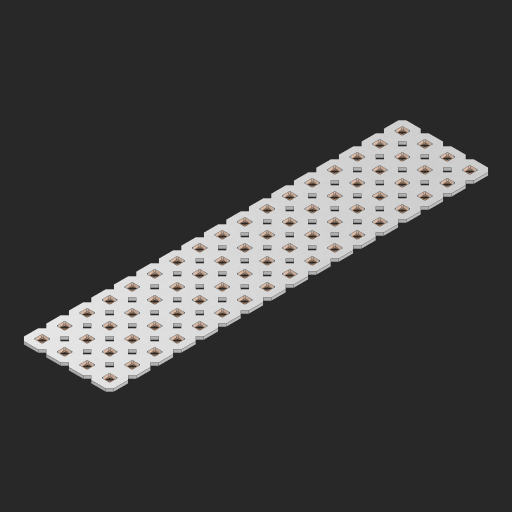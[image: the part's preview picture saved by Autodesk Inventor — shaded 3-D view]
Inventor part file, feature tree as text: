
AUTODESK INVENTOR PART (.ipt)
format: ipt  version: 2023 (Build 270158000, 158)  size: 1,068,544 bytes
history: native  units: in
note: dims shown in document units (in); Inventor stores cm internally (conversion verified against a paired STEP export)
features: other x69, extrude x67, sketch x2, pattern_linear x1
ambient origin geometry x8: Origin, YZ Plane, XZ Plane, XY Plane, X Axis, Y Axis, Z Axis, Center Point
bodies: Solid1 (feature_tree), Body (feature_tree)
feature tree (139):
  pattern_linear  "Rectangular Pattern1"  Spacing1=0.09in  [1 undecoded]
  sketch  "Sketch1"  dims[d1=0.5in]
  sketch  "Sketch2"  dims[d2=0.182in d3=0.09in d4=0.09in d5=0.09in d6=0.09in d7=0.09in d8=0.09in d9=0.09in d10=0.09in d11=0.02in d13=0.0in d14=0.172in d15=0.0625in d16=0.0in d19=0.5in d22=0.5in]
  other  "Srf1"
  other  "Srf126"
  other  "Srf127"
  other  "Srf128"
  other  "Srf129"
  other  "Srf130"
  other  "Srf131"
  other  "Srf250"
  other  "Srf251"
  other  "Srf252"
  other  "Srf253"
  other  "Srf254"
  other  "Srf255"
  other  "Srf256"
  other  "Srf257"
  other  "Srf258"
  other  "Srf259"
  other  "Srf268"
  other  "Srf269"
  other  "Srf270"
  other  "Srf271"
  other  "Srf272"
  other  "Srf273"
  other  "Srf274"
  other  "Srf275"
  other  "Srf276"
  other  "Srf277"
  other  "Srf278"
  other  "Srf279"
  other  "Srf280"
  other  "Srf281"
  other  "Srf282"
  other  "Srf283"
  other  "Srf284"
  other  "Srf293"
  other  "Srf294"
  other  "Srf295"
  other  "Srf296"
  other  "Srf297"
  other  "Srf298"
  other  "Srf299"
  other  "Srf300"
  other  "Srf301"
  other  "Srf302"
  other  "Srf303"
  other  "Srf304"
  other  "Srf305"
  other  "Srf306"
  other  "Srf307"
  other  "Srf308"
  other  "Srf309"
  other  "Srf318"
  other  "Srf319"
  other  "Srf320"
  other  "Srf321"
  other  "Srf322"
  other  "Srf323"
  other  "Srf324"
  other  "Srf325"
  other  "Srf326"
  other  "Srf327"
  other  "Srf328"
  other  "Srf329"
  other  "Srf330"
  other  "Srf331"
  other  "Srf332"
  other  "Srf333"
  other  "Srf334"
  other  "Circle"
  extrude  "ExtrusionSrf126"  Depth=0.09in
  extrude  "ExtrusionSrf127"  Depth=0.09in
  extrude  "ExtrusionSrf128"  Depth=0.09in
  extrude  "ExtrusionSrf129"  Depth=0.09in
  extrude  "ExtrusionSrf130"  Depth=0.09in
  extrude  "ExtrusionSrf131"  Depth=0.09in
  extrude  "ExtrusionSrf250"  Depth=0.09in
  extrude  "ExtrusionSrf251"  Depth=0.02in
  extrude  "ExtrusionSrf252"  TaperAngle=0.0deg  [1 undecoded]
  extrude  "ExtrusionSrf253"  Depth=0.5in
  extrude  "ExtrusionSrf254"  Depth=0.0625in TaperAngle=0.0deg
  extrude  "ExtrusionSrf255"  Depth=0.5in
  extrude  "ExtrusionSrf256"  Depth=0.5in
  extrude  "ExtrusionSrf257"  [1 undecoded]
  extrude  "ExtrusionSrf258"  [1 undecoded]
  extrude  "ExtrusionSrf259"  [1 undecoded]
  extrude  "ExtrusionSrf268"  [1 undecoded]
  extrude  "ExtrusionSrf269"  [1 undecoded]
  extrude  "ExtrusionSrf270"  [1 undecoded]
  extrude  "ExtrusionSrf271"  [1 undecoded]
  extrude  "ExtrusionSrf272"  [1 undecoded]
  extrude  "ExtrusionSrf273"  [1 undecoded]
  extrude  "ExtrusionSrf274"  [1 undecoded]
  extrude  "ExtrusionSrf275"  [1 undecoded]
  extrude  "ExtrusionSrf276"  [1 undecoded]
  extrude  "ExtrusionSrf277"  [1 undecoded]
  extrude  "ExtrusionSrf278"  [1 undecoded]
  extrude  "ExtrusionSrf279"  [1 undecoded]
  extrude  "ExtrusionSrf280"  [1 undecoded]
  extrude  "ExtrusionSrf281"  [1 undecoded]
  extrude  "ExtrusionSrf282"  [1 undecoded]
  extrude  "ExtrusionSrf283"  [1 undecoded]
  extrude  "ExtrusionSrf284"  [1 undecoded]
  extrude  "ExtrusionSrf293"  [1 undecoded]
  extrude  "ExtrusionSrf294"  [1 undecoded]
  extrude  "ExtrusionSrf295"  [1 undecoded]
  extrude  "ExtrusionSrf296"  [1 undecoded]
  extrude  "ExtrusionSrf297"  [1 undecoded]
  extrude  "ExtrusionSrf298"  [1 undecoded]
  extrude  "ExtrusionSrf299"  [1 undecoded]
  extrude  "ExtrusionSrf300"  [1 undecoded]
  extrude  "ExtrusionSrf301"  [1 undecoded]
  extrude  "ExtrusionSrf302"  [1 undecoded]
  extrude  "ExtrusionSrf303"  [1 undecoded]
  extrude  "ExtrusionSrf304"  [1 undecoded]
  extrude  "ExtrusionSrf305"  [1 undecoded]
  extrude  "ExtrusionSrf306"  [1 undecoded]
  extrude  "ExtrusionSrf307"  [1 undecoded]
  extrude  "ExtrusionSrf308"  [1 undecoded]
  extrude  "ExtrusionSrf309"  [1 undecoded]
  extrude  "ExtrusionSrf318"  [1 undecoded]
  extrude  "ExtrusionSrf319"  [1 undecoded]
  extrude  "ExtrusionSrf320"  [1 undecoded]
  extrude  "ExtrusionSrf321"  [1 undecoded]
  extrude  "ExtrusionSrf322"  [1 undecoded]
  extrude  "ExtrusionSrf323"  [1 undecoded]
  extrude  "ExtrusionSrf324"  [1 undecoded]
  extrude  "ExtrusionSrf325"  [1 undecoded]
  extrude  "ExtrusionSrf326"  [1 undecoded]
  extrude  "ExtrusionSrf327"  [1 undecoded]
  extrude  "ExtrusionSrf328"  [1 undecoded]
  extrude  "ExtrusionSrf329"  [1 undecoded]
  extrude  "ExtrusionSrf330"  [1 undecoded]
  extrude  "ExtrusionSrf331"  [1 undecoded]
  extrude  "ExtrusionSrf332"  [1 undecoded]
  extrude  "ExtrusionSrf333"  [1 undecoded]
  extrude  "ExtrusionSrf334"  [1 undecoded]
note: 56 required parameter values undecoded (feature->parameter linkage not recoverable at this tier; creation-order binding heuristic only, values carry confidence <= 0.55)
